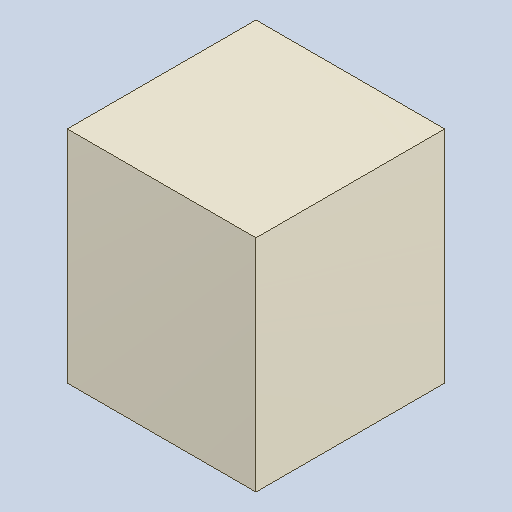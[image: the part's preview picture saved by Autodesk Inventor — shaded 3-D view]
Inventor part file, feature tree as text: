
AUTODESK INVENTOR PART (.ipt)
format: ipt  version: 2023.4 (Build 274418000, 418)  size: 82,944 bytes
history: native  units: mm
features: extrude x1
ambient origin geometry x8: Origin, YZ Plane, XZ Plane, XY Plane, X Axis, Y Axis, Z Axis, Center Point
bodies: Solid1 (feature_tree)
feature tree (1):
  extrude  "Extruded_26"  [1 undecoded]
note: 1 required parameter value undecoded (feature->parameter linkage not recoverable at this tier; creation-order binding heuristic only, values carry confidence <= 0.55)
